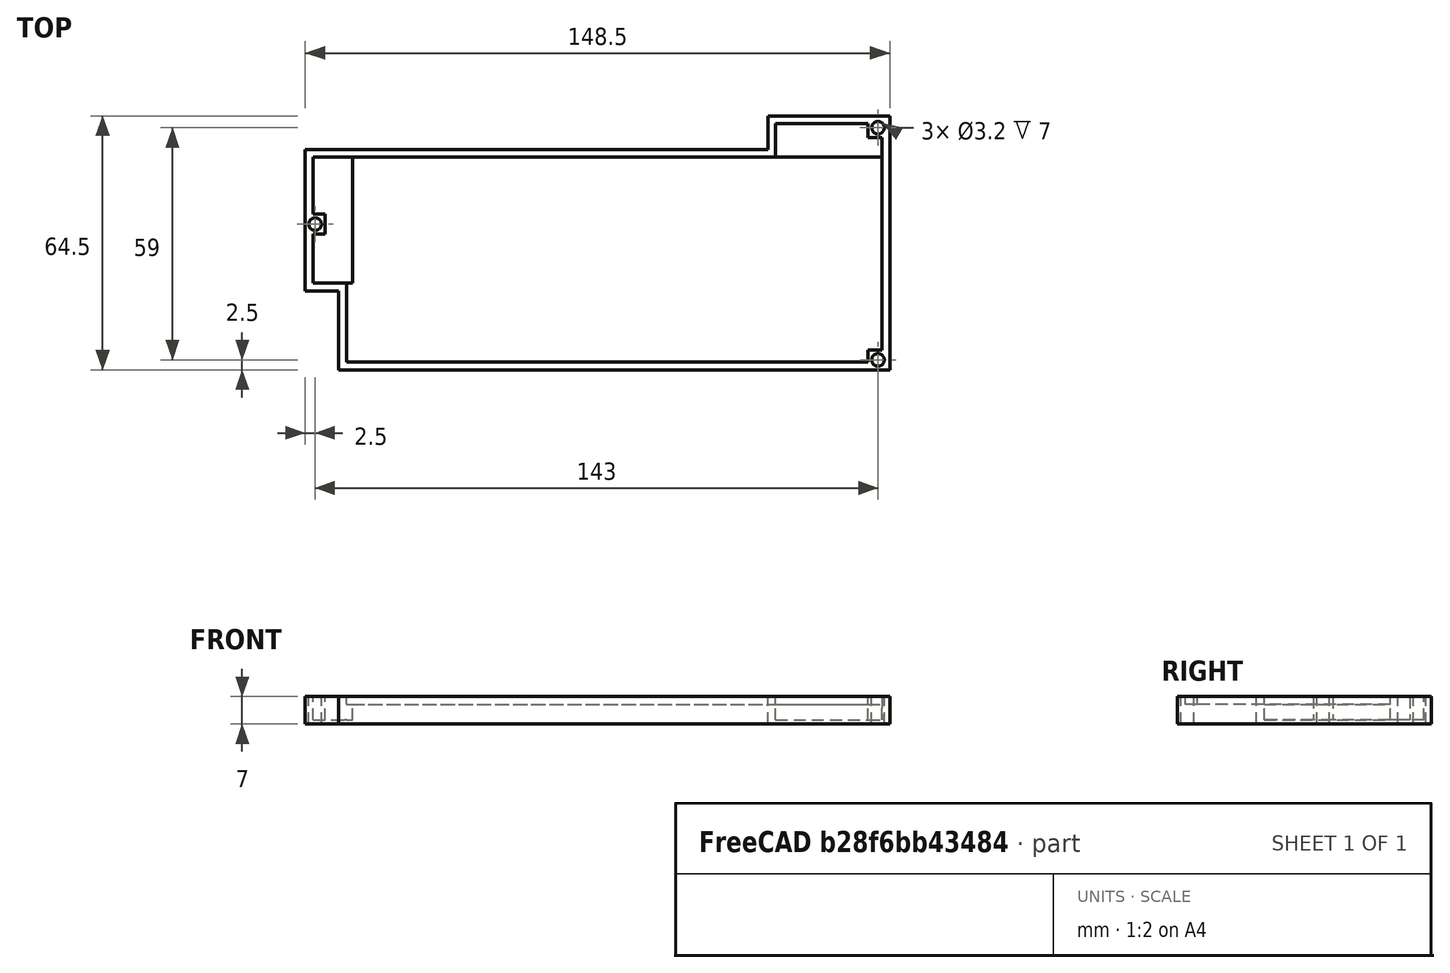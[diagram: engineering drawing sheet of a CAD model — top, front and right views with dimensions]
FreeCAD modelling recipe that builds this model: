
FCSTD DOCUMENT  (FreeCAD 0.19R24291 (Git))
Label: cover_B
License: All rights reserved
LicenseURL: http://en.wikipedia.org/wiki/All_rights_reserved
objects: Part::Box×14, Part::MultiFuse×5, Part::Cylinder×3, Part::Cut×3
note: 25 computed .brp shape members not serialized (recipe doc carries the construction recipe); baked Part::Feature solids carry a one-line shape summary decoded from their .brp

FEATURE [Part::Box] Box  label="Cube"
  AttacherType = Attacher::AttachEngine3D
  Height = 7
  Length = 148.5
  Width = 64.5
FEATURE [Part::Box] Box001  label="Cube001"
  AttacherType = Attacher::AttachEngine3D
  Height = 7
  Length = 8.5
  Width = 20
FEATURE [Part::Box] Box002  label="Cube002"
  AttacherType = Attacher::AttachEngine3D
  Height = 7
  Length = 117.5
  Placement = pos=(0,56,0) rot=(0,0,1;0rad)
  Width = 8.5
FEATURE [Part::Cylinder] Cylinder
  Angle = 360
  AttacherType = Attacher::AttachEngine3D
  Height = 10
  Placement = pos=(145.5,2.5,0) rot=(0,0,1;0rad)
  Radius = 1.6
FEATURE [Part::Cylinder] Cylinder001
  Angle = 360
  AttacherType = Attacher::AttachEngine3D
  Height = 10
  Placement = pos=(145.5,61.5,0) rot=(0,0,1;0rad)
  Radius = 1.6
FEATURE [Part::Cylinder] Cylinder002
  Angle = 360
  AttacherType = Attacher::AttachEngine3D
  Height = 10
  Placement = pos=(2.5,37,0) rot=(0,0,1;0rad)
  Radius = 1.6
FEATURE [Part::Box] Box003  label="Cube003"
  AttacherType = Attacher::AttachEngine3D
  Height = 7
  Length = 136
  Placement = pos=(10.5,2,0) rot=(0,0,1;0rad)
  Width = 52
FEATURE [Part::Box] Box004  label="Cube004"
  AttacherType = Attacher::AttachEngine3D
  Height = 7
  Length = 8.5
  Placement = pos=(2,22,0) rot=(0,0,1;0rad)
  Width = 32
FEATURE [Part::Box] Box005  label="Cube005"
  AttacherType = Attacher::AttachEngine3D
  Height = 7
  Length = 27
  Placement = pos=(119.5,54,0) rot=(0,0,1;0rad)
  Width = 8.5
FEATURE [Part::Box] Box006  label="Cube006"
  AttacherType = Attacher::AttachEngine3D
  Height = 7
  Length = 5
  Placement = pos=(0,34.5,0) rot=(0,0,1;0rad)
  Width = 5
FEATURE [Part::Box] Box007  label="Cube007"
  AttacherType = Attacher::AttachEngine3D
  Height = 7
  Length = 5
  Placement = pos=(143,59,0) rot=(0,0,1;0rad)
  Width = 5
FEATURE [Part::Box] Box008  label="Cube008"
  AttacherType = Attacher::AttachEngine3D
  Height = 7
  Length = 5
  Placement = pos=(143,0,0) rot=(0,0,1;0rad)
  Width = 5
FEATURE [Part::MultiFuse] Fusion
  Shapes = -> [Box002,Box001]
FEATURE [Part::Cut] Cut
  Base = -> Box
  Tool = -> Fusion
FEATURE [Part::MultiFuse] Fusion001
  Shapes = -> [Box003,Box004,Box005]
FEATURE [Part::MultiFuse] Fusion003
  Shapes = -> [Cylinder002,Cylinder001,Cylinder]
FEATURE [Part::Cut] Cut001
  Base = -> Cut
  Tool = -> Fusion001
FEATURE [Part::MultiFuse] Fusion002
  Shapes = -> [Box006,Box007,Box008,Cut001]
FEATURE [Part::Box] Box009  label="Cube009"
  AttacherType = Attacher::AttachEngine3D
  Height = 1
  Length = 139
  Placement = pos=(9,0,0) rot=(0,0,1;0rad)
  Width = 55
FEATURE [Part::Box] Box010  label="Cube010"
  AttacherType = Attacher::AttachEngine3D
  Height = 1
  Length = 9
  Placement = pos=(1,21,0) rot=(0,0,1;0rad)
  Width = 34
FEATURE [Part::Box] Box011  label="Cube011"
  AttacherType = Attacher::AttachEngine3D
  Height = 1
  Length = 28
  Placement = pos=(119,54,0) rot=(0,0,1;0rad)
  Width = 10
FEATURE [Part::Box] Box012  label="Cube012"
  AttacherType = Attacher::AttachEngine3D
  Height = 5
  Length = 135
  Placement = pos=(12,0,0) rot=(0,0,1;0rad)
  Width = 54
FEATURE [Part::Box] Box013  label="Cube013"
  AttacherType = Attacher::AttachEngine3D
  Height = 5
  Length = 6
  Placement = pos=(10,0,0) rot=(0,0,1;0rad)
  Width = 22
FEATURE [Part::MultiFuse] Fusion004
  Shapes = -> [Fusion002,Box009,Box010,Box011,Box012,Box013]
FEATURE [Part::Cut] Cut002
  Base = -> Fusion004
  Tool = -> Fusion003
